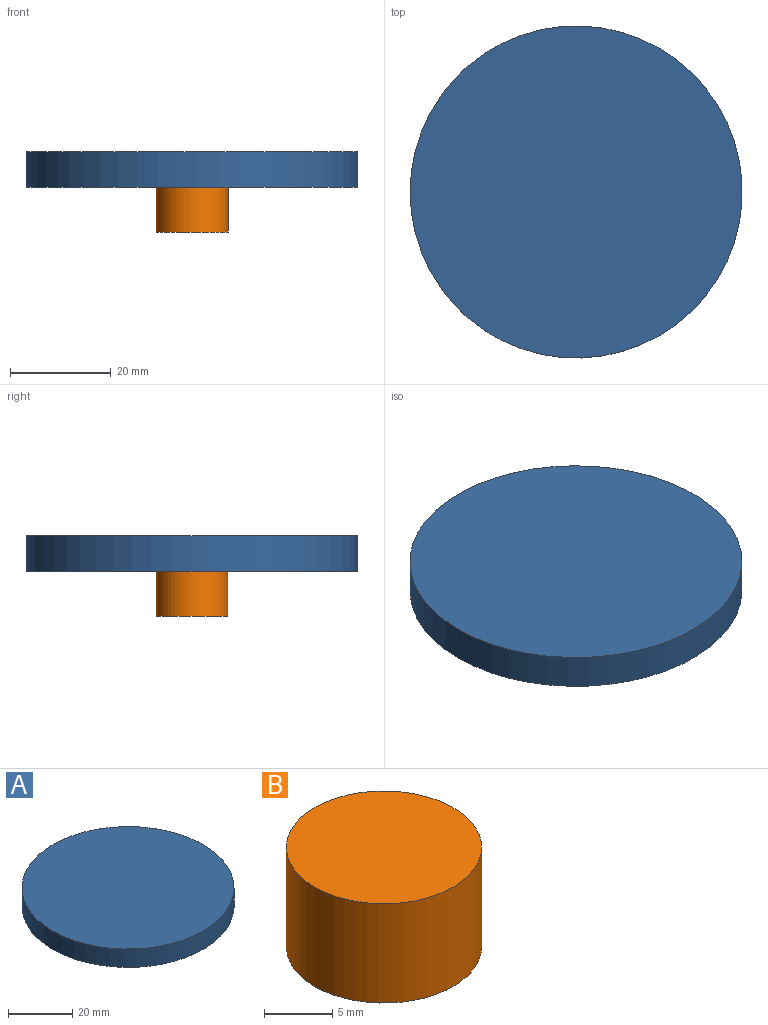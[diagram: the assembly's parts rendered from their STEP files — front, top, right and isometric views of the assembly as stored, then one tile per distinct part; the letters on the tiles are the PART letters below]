
ASSEMBLY  parts=2 mates=1
PART A: 3 faces, bbox 66x66x7 mm
  f0: plane 66x66mm, normal (0,0,-1), area 3421.2mm2, adj f2
  f1: plane 66x66mm, normal (0,0,1), area 3421.2mm2, adj f2
  f2: cylinder r=33mm len=66mm, axis (0,0,-1), area 1451.4mm2, adj f0,f1
PART B: 3 faces, bbox 14.3x14.3x8.9 mm
  f0: plane 14.3x14.3mm, normal (0,0,-1), area 160.6mm2, adj f2
  f1: plane 14.3x14.3mm, normal (0,0,1), area 160.6mm2, adj f2
  f2: cylinder r=7.15mm len=14.3mm, axis (0,0,-1), area 399.8mm2, adj f0,f1
PLACE A t=(0,0,8.9)mm
PLACE B at identity
MATE fastened A.f2 <-> B.f2  axis (0,0,-1) through (0,0,8.9)mm
